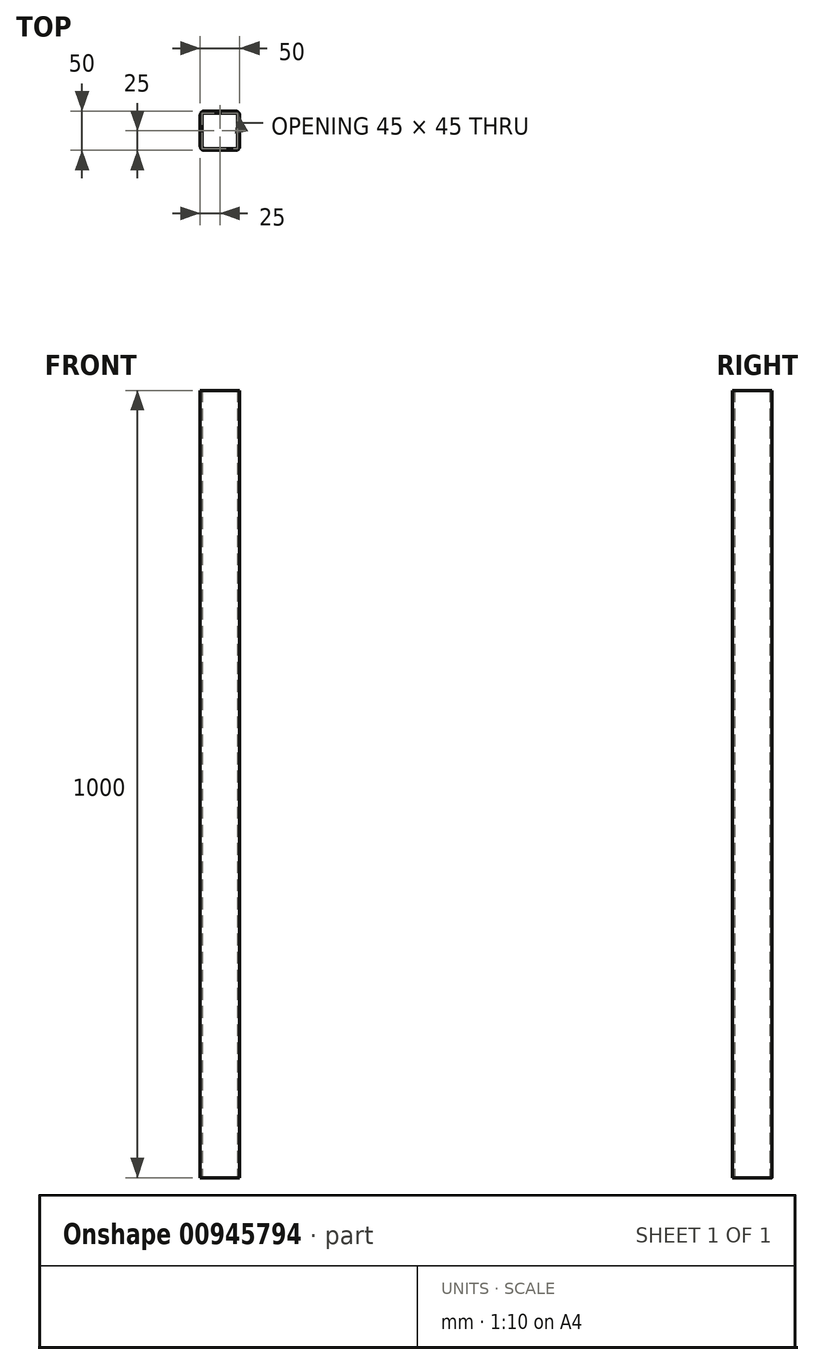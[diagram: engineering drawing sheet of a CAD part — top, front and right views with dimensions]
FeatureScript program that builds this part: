
annotation { "Feature Type Name" : "Feature", "Feature Type Description" : "" }
export const myFeature = defineFeature(function(context is Context, id is Id, definition is map)
    precondition{}
    {
        {
            var Q0;
            Q0=qCreatedBy(makeId("Top.planeOp"),FACE);
            var sketch = newSketch(context, id + "F0", { "sketchPlane" : qUnion([Q0])});
            skLineSegment(sketch, "E0.bottom", {"start": v(20, 25) * mm, "end": v(-20, 25) * mm});
            skLineSegment(sketch, "E0.top", {"start": v(20, -25) * mm, "end": v(-20, -25) * mm});
            skLineSegment(sketch, "E0.left", {"start": v(25, 20) * mm, "end": v(25, -20) * mm});
            skLineSegment(sketch, "E0.right", {"start": v(-25, 20) * mm, "end": v(-25, -20) * mm});
            skPoint(sketch, "E0.middle", {"position": v(0, 0) * mm});
            skPoint(sketch, "E1.visualSharp", {"position": v(-25, 25) * mm});
            skArc(sketch, "E1.filletArc", {"start": v(-20, 25) * mm, "mid": v(-23.54, 23.54) * mm, "end": v(-25, 20) * mm});
            skPoint(sketch, "E2.visualSharp", {"position": v(25, 25) * mm});
            skArc(sketch, "E2.filletArc", {"start": v(25, 20) * mm, "mid": v(23.54, 23.54) * mm, "end": v(20, 25) * mm});
            skPoint(sketch, "E3.visualSharp", {"position": v(25, -25) * mm});
            skArc(sketch, "E3.filletArc", {"start": v(20, -25) * mm, "mid": v(23.54, -23.54) * mm, "end": v(25, -20) * mm});
            skPoint(sketch, "E4.visualSharp", {"position": v(-25, -25) * mm});
            skArc(sketch, "E4.filletArc", {"start": v(-25, -20) * mm, "mid": v(-23.54, -23.54) * mm, "end": v(-20, -25) * mm});
            skArc(sketch, "E5.0", {"start": v(22.5, 20) * mm, "mid": v(21.77, 21.77) * mm, "end": v(20, 22.5) * mm});
            skLineSegment(sketch, "E5.1", {"start": v(22.5, 20) * mm, "end": v(22.5, -20) * mm});
            skLineSegment(sketch, "E5.2", {"start": v(20, 22.5) * mm, "end": v(-20, 22.5) * mm});
            skArc(sketch, "E5.3", {"start": v(20, -22.5) * mm, "mid": v(21.77, -21.77) * mm, "end": v(22.5, -20) * mm});
            skArc(sketch, "E5.4", {"start": v(-20, 22.5) * mm, "mid": v(-21.77, 21.77) * mm, "end": v(-22.5, 20) * mm});
            skLineSegment(sketch, "E5.5", {"start": v(-22.5, 20) * mm, "end": v(-22.5, -20) * mm});
            skArc(sketch, "E5.6", {"start": v(-22.5, -20) * mm, "mid": v(-21.77, -21.77) * mm, "end": v(-20, -22.5) * mm});
            skLineSegment(sketch, "E5.7", {"start": v(20, -22.5) * mm, "end": v(-20, -22.5) * mm});
            skSolve(sketch);
        }
        {
            var Q0;
            Q0 = qSketchRegion(id + "F0", true);
            extrude(context, id + "F1", {"entities" : qUnion([Q0]), "depth" : 1000 * mm, "offsetDistance" : 25 * mm});
        }
    });
